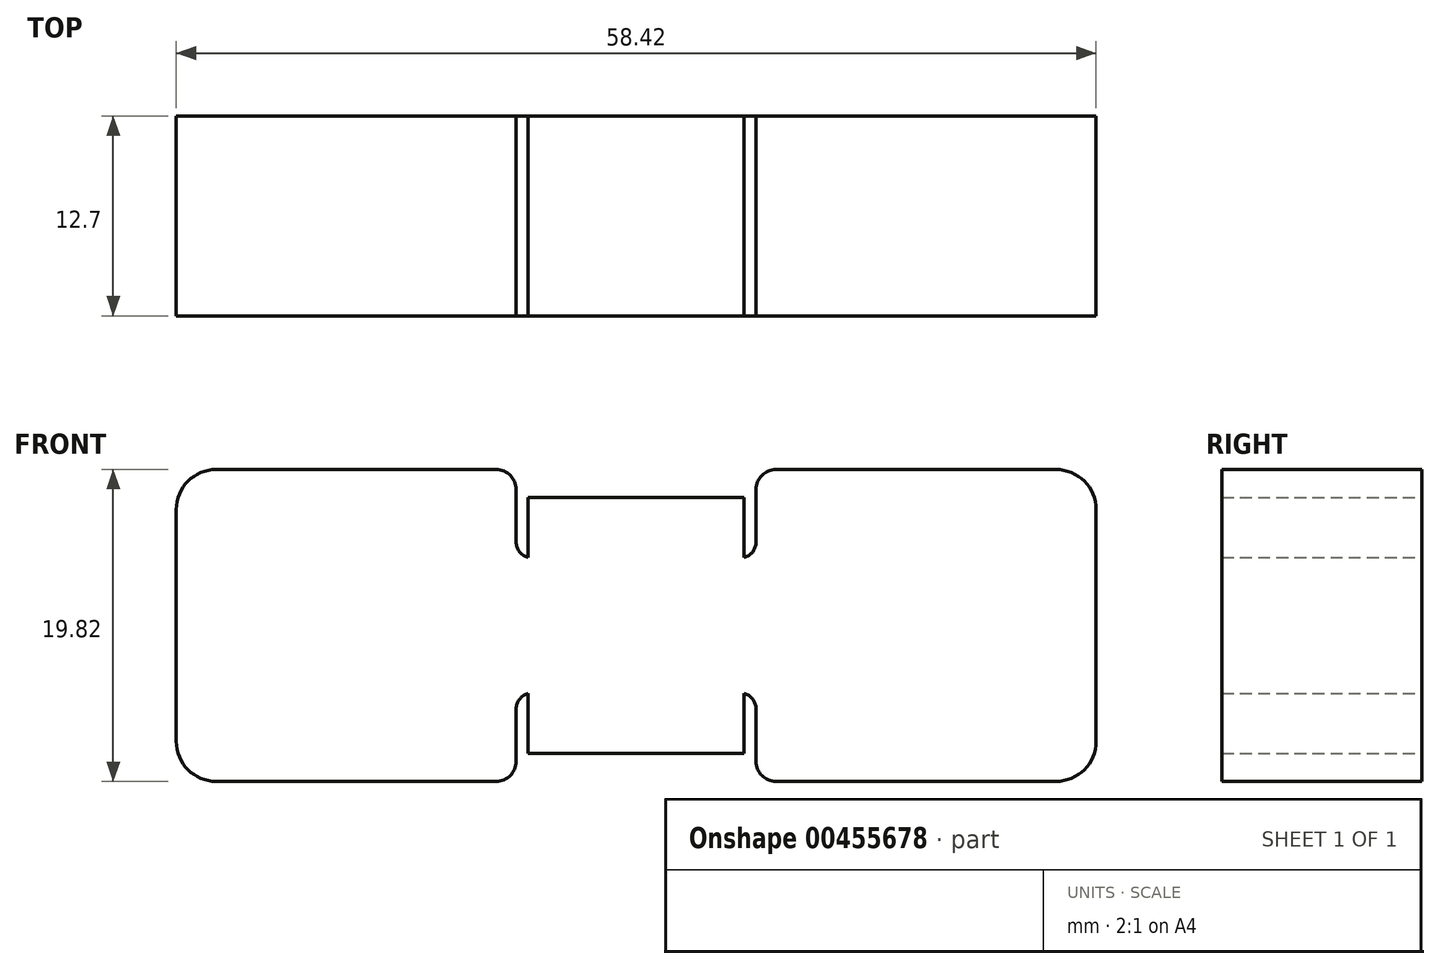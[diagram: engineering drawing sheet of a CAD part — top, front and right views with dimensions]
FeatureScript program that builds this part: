
annotation { "Feature Type Name" : "Feature", "Feature Type Description" : "" }
export const myFeature = defineFeature(function(context is Context, id is Id, definition is map)
    precondition{}
    {
        {
            var Q0;
            Q0=qCreatedBy(makeId("Front.planeOp"),FACE);
            var sketch = newSketch(context, id + "F0", { "sketchPlane" : qUnion([Q0])});
            skLineSegment(sketch, "E0", {"start": v(0, 0) * mm, "end": v(-29.21, 0) * mm});
            skLineSegment(sketch, "E1", {"start": v(-29.21, 0) * mm, "end": v(-29.21, 9.9) * mm});
            skLineSegment(sketch, "E2", {"start": v(0, 0) * mm, "end": v(0, 8.13) * mm});
            skLineSegment(sketch, "E3", {"start": v(0, 8.13) * mm, "end": v(-6.86, 8.13) * mm});
            skLineSegment(sketch, "E4", {"start": v(-29.21, 9.9) * mm, "end": v(-7.62, 9.9) * mm});
            skLineSegment(sketch, "E5", {"start": v(-7.62, 9.9) * mm, "end": v(-7.62, 4.32) * mm});
            skLineSegment(sketch, "E6", {"start": v(-7.62, 4.32) * mm, "end": v(-6.85, 4.32) * mm});
            skLineSegment(sketch, "E7", {"start": v(-6.85, 4.32) * mm, "end": v(-6.85, 4.99) * mm});
            skLineSegment(sketch, "E8", {"start": v(-6.86, 8.13) * mm, "end": v(-6.85, 4.32) * mm});
            skSolve(sketch);
        }
        {
            var Q0;
            Q0=makeQuery(id+"F0.imprint","IMPRINT",FACE,{"disambiguationData":[TD([[makeQuery(id+"F0.imprint","IMPRINT",EDGE,{"derivedFrom":sQuery(id+"F0.wireOp",EDGE,"E0")}),-1.0]])]});
            extrude(context, id + "F1", {"entities" : qUnion([Q0]), "depth" : 12.7 * mm});
        }
        {
            var Q0;
            Q0=makeQuery(id+"F1.opExtrude","SWEPT_EDGE",EDGE,{"disambiguationData":[OSD([sQuery(id+"F0.wireOp",EDGE,"E1"),sQuery(id+"F0.wireOp",EDGE,"E4")])]});
            fillet(context, id + "F2", {"entities" : qUnion([Q0]), "radius" : 2.54 * mm, "tangentPropagation" : true, "allowEdgeOverflow" : false});
        }
        {
            var Q0;
            Q0=makeQuery(id+"F1.opExtrude","SWEPT_EDGE",EDGE,{"disambiguationData":[OSD([sQuery(id+"F0.wireOp",EDGE,"E4"),sQuery(id+"F0.wireOp",EDGE,"E5")])]});
            fillet(context, id + "F3", {"entities" : qUnion([Q0]), "radius" : 1.27 * mm, "tangentPropagation" : true, "allowEdgeOverflow" : false});
        }
        {
            var Q0;
            Q0=makeQuery(id+"F1.opExtrude","SWEPT_EDGE",EDGE,{"disambiguationData":[OSD([sQuery(id+"F0.wireOp",EDGE,"E5"),sQuery(id+"F0.wireOp",EDGE,"E6")])]});
            fillet(context, id + "F4", {"entities" : qUnion([Q0]), "radius" : 1.02 * mm, "tangentPropagation" : true, "allowEdgeOverflow" : false});
        }
        {
            var Q0;
            Q0=makeQuery(id+"F1.opExtrude","SWEPT_BODY",BODY,{"disambiguationData":[OSD([sQuery(id+"F0.wireOp",EDGE,"E0"),sQuery(id+"F0.wireOp",EDGE,"E1"),sQuery(id+"F0.wireOp",EDGE,"E2"),sQuery(id+"F0.wireOp",EDGE,"E3"),sQuery(id+"F0.wireOp",EDGE,"E4"),sQuery(id+"F0.wireOp",EDGE,"E5"),sQuery(id+"F0.wireOp",EDGE,"E6"),sQuery(id+"F0.wireOp",EDGE,"E8")])]});
            var Q1;
            Q1=makeQuery(id+"F1.opExtrude","SWEPT_FACE",FACE,{"disambiguationData":[OSD([sQuery(id+"F0.wireOp",EDGE,"E0")])]});
            mirror(context, id + "F5", {"operationType" : NewBodyOperationType.ADD, "entities" : qUnion([Q0]), "mirrorPlane" : qUnion([Q1])});
        }
        {
            var Q0;
            Q0=makeQuery(id+"F1.opExtrude","SWEPT_BODY",BODY,{"disambiguationData":[OSD([sQuery(id+"F0.wireOp",EDGE,"E0"),sQuery(id+"F0.wireOp",EDGE,"E1"),sQuery(id+"F0.wireOp",EDGE,"E2"),sQuery(id+"F0.wireOp",EDGE,"E3"),sQuery(id+"F0.wireOp",EDGE,"E4"),sQuery(id+"F0.wireOp",EDGE,"E5"),sQuery(id+"F0.wireOp",EDGE,"E6"),sQuery(id+"F0.wireOp",EDGE,"E8")])]});
            var Q1;
            {var subQ0=makeQuery(id+"F1.opExtrude","SWEPT_FACE",FACE,{"disambiguationData":[OSD([sQuery(id+"F0.wireOp",EDGE,"E2")])]});Q1=makeQuery(id+"F5.boolean.opBoolean","MERGE",FACE,{"derivedFrom":[subQ0,makeQuery(id+"F5.opPattern","COPY",FACE,{"derivedFrom":subQ0,"instanceName":"1"})]});}
            mirror(context, id + "F6", {"operationType" : NewBodyOperationType.ADD, "entities" : qUnion([Q0]), "mirrorPlane" : qUnion([Q1])});
        }
    });
